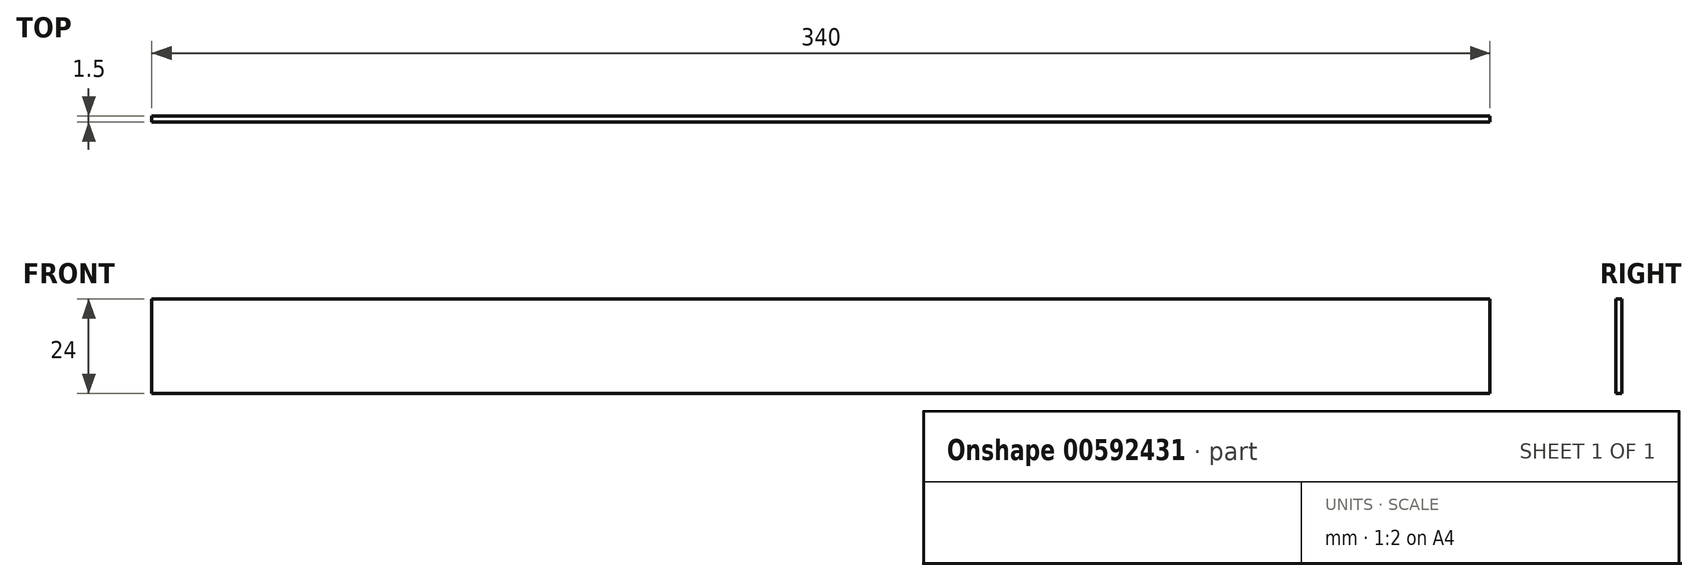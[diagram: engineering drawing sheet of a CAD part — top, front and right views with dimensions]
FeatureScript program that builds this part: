
annotation { "Feature Type Name" : "Feature", "Feature Type Description" : "" }
export const myFeature = defineFeature(function(context is Context, id is Id, definition is map)
    precondition{}
    {
        {
            var Q0;
            Q0=qCreatedBy(makeId("Right.planeOp"),FACE);
            var sketch = newSketch(context, id + "F0", { "sketchPlane" : qUnion([Q0])});
            skCircle(sketch, "E0", {"center": v(0, 0) * mm, "radius": 3 * mm});
            skSolve(sketch);
        }
        {
            var Q0;
            Q0=sQuery(id+"F0.wireOp",EDGE,"E0");
            extrude(context, id + "F1", {"bodyType" : ToolBodyType.SURFACE, "surfaceEntities" : qUnion([Q0]), "oppositeDirection" : true, "depth" : 340 * mm, "offsetDistance" : 25 * mm});
        }
        {
            var Q0;
            Q0=qCreatedBy(makeId("Right.planeOp"),FACE);
            var sketch = newSketch(context, id + "F2", { "sketchPlane" : qUnion([Q0])});
            skLineSegment(sketch, "E1", {"start": v(0, 0) * mm, "end": v(0, -12) * mm});
            skLineSegment(sketch, "E2", {"start": v(0, -12) * mm, "end": v(1.5, -12) * mm});
            skLineSegment(sketch, "E3", {"start": v(1.5, -12) * mm, "end": v(1.5, 12) * mm});
            skLineSegment(sketch, "E4", {"start": v(1.5, 12) * mm, "end": v(0, 12) * mm});
            skLineSegment(sketch, "E5", {"start": v(0, 12) * mm, "end": v(0, 0) * mm});
            skSolve(sketch);
        }
        {
            var Q0;
            Q0=makeQuery(id+"F2.imprint","IMPRINT",FACE,{"disambiguationData":[TD([[makeQuery(id+"F2.imprint","IMPRINT",EDGE,{"derivedFrom":sQuery(id+"F2.wireOp",EDGE,"E1")}),1.0]])]});
            extrude(context, id + "F3", {"entities" : qUnion([Q0]), "oppositeDirection" : true, "depth" : 340 * mm, "offsetDistance" : 25 * mm});
        }
    });
